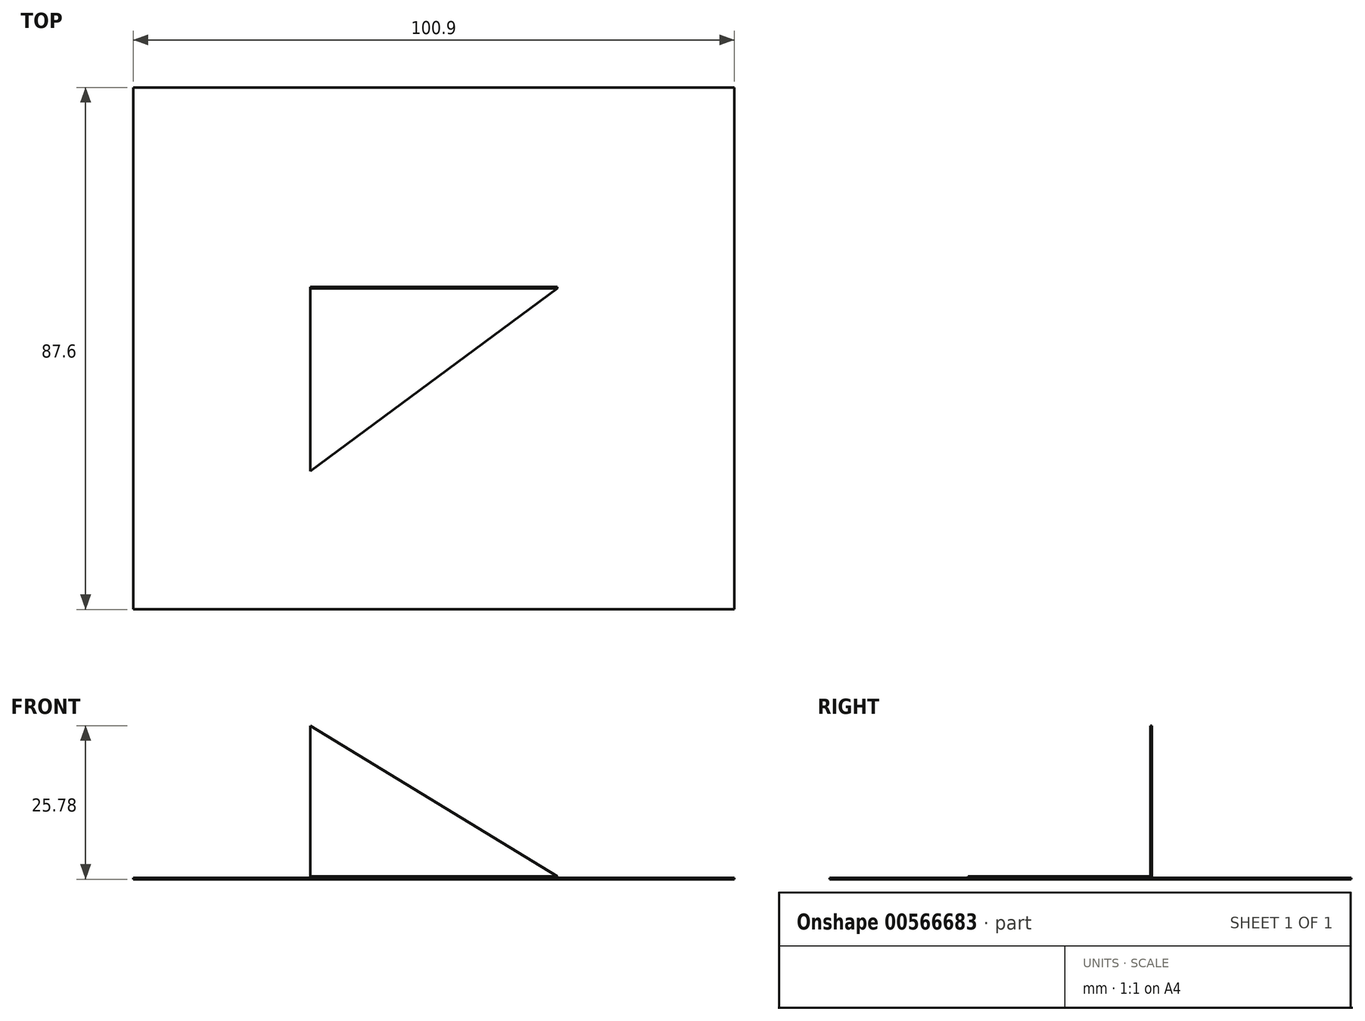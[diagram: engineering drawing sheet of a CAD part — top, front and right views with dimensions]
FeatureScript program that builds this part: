
annotation { "Feature Type Name" : "Feature", "Feature Type Description" : "" }
export const myFeature = defineFeature(function(context is Context, id is Id, definition is map)
    precondition{}
    {
        {
            var Q0;
            Q0=qCreatedBy(makeId("Top.planeOp"),FACE);
            var sketch = newSketch(context, id + "F0", { "sketchPlane" : qUnion([Q0])});
            skLineSegment(sketch, "E0.bottom", {"start": v(50.45, -43.8) * mm, "end": v(-50.45, -43.8) * mm});
            skLineSegment(sketch, "E0.top", {"start": v(50.45, 43.8) * mm, "end": v(-50.45, 43.8) * mm});
            skLineSegment(sketch, "E0.left", {"start": v(50.45, -43.8) * mm, "end": v(50.45, 43.8) * mm});
            skLineSegment(sketch, "E0.right", {"start": v(-50.45, -43.8) * mm, "end": v(-50.45, 43.8) * mm});
            skPoint(sketch, "E0.middle", {"position": v(0, 0) * mm});
            skSolve(sketch);
        }
        {
            var Q0;
            Q0 = qSketchRegion(id + "F0", true);
            extrude(context, id + "F1", {"entities" : qUnion([Q0]), "depth" : 0.25 * mm, "offsetDistance" : 25.4 * mm});
        }
        {
            var Q0;
            Q0=makeQuery(id+"F1.opExtrude","CAP_FACE",FACE,{"disambiguationData":[OSD([sQuery(id+"F0.wireOp",EDGE,"E0.bottom"),sQuery(id+"F0.wireOp",EDGE,"E0.top"),sQuery(id+"F0.wireOp",EDGE,"E0.left"),sQuery(id+"F0.wireOp",EDGE,"E0.right")])],"isStart":false});
            var sketch = newSketch(context, id + "F2", { "sketchPlane" : qUnion([Q0])});
            skLineSegment(sketch, "E1", {"start": v(-20.74, 10.06) * mm, "end": v(20.74, 10.06) * mm});
            skLineSegment(sketch, "E2", {"start": v(-20.74, 10.06) * mm, "end": v(-20.74, -20.58) * mm});
            skLineSegment(sketch, "E3", {"start": v(-20.74, -20.58) * mm, "end": v(20.74, 10.06) * mm});
            skSolve(sketch);
        }
        {
            var Q0;
            Q0 = qSketchRegion(id + "F2", true);
            extrude(context, id + "F3", {"entities" : qUnion([Q0]), "operationType" : NewBodyOperationType.ADD, "depth" : 0.25 * mm, "offsetDistance" : 25.4 * mm});
        }
        {
            var Q0;
            Q0=makeQuery(id+"F3.opExtrude","SWEPT_FACE",FACE,{"disambiguationData":[OSD([sQuery(id+"F2.wireOp",EDGE,"E1")])]});
            var sketch = newSketch(context, id + "F4", { "sketchPlane" : qUnion([Q0])});
            skLineSegment(sketch, "E4", {"start": v(20.74, 0.5) * mm, "end": v(20.74, 25.78) * mm});
            skLineSegment(sketch, "E5", {"start": v(20.74, 25.78) * mm, "end": v(-20.74, 0.5) * mm});
            skLineSegment(sketch, "E6", {"start": v(-20.74, 0.5) * mm, "end": v(20.74, 0.5) * mm});
            skSolve(sketch);
        }
        {
            var Q0;
            Q0 = qSketchRegion(id + "F4", true);
            extrude(context, id + "F5", {"entities" : qUnion([Q0]), "depth" : 0.25 * mm, "offsetDistance" : 25.4 * mm});
        }
    });
